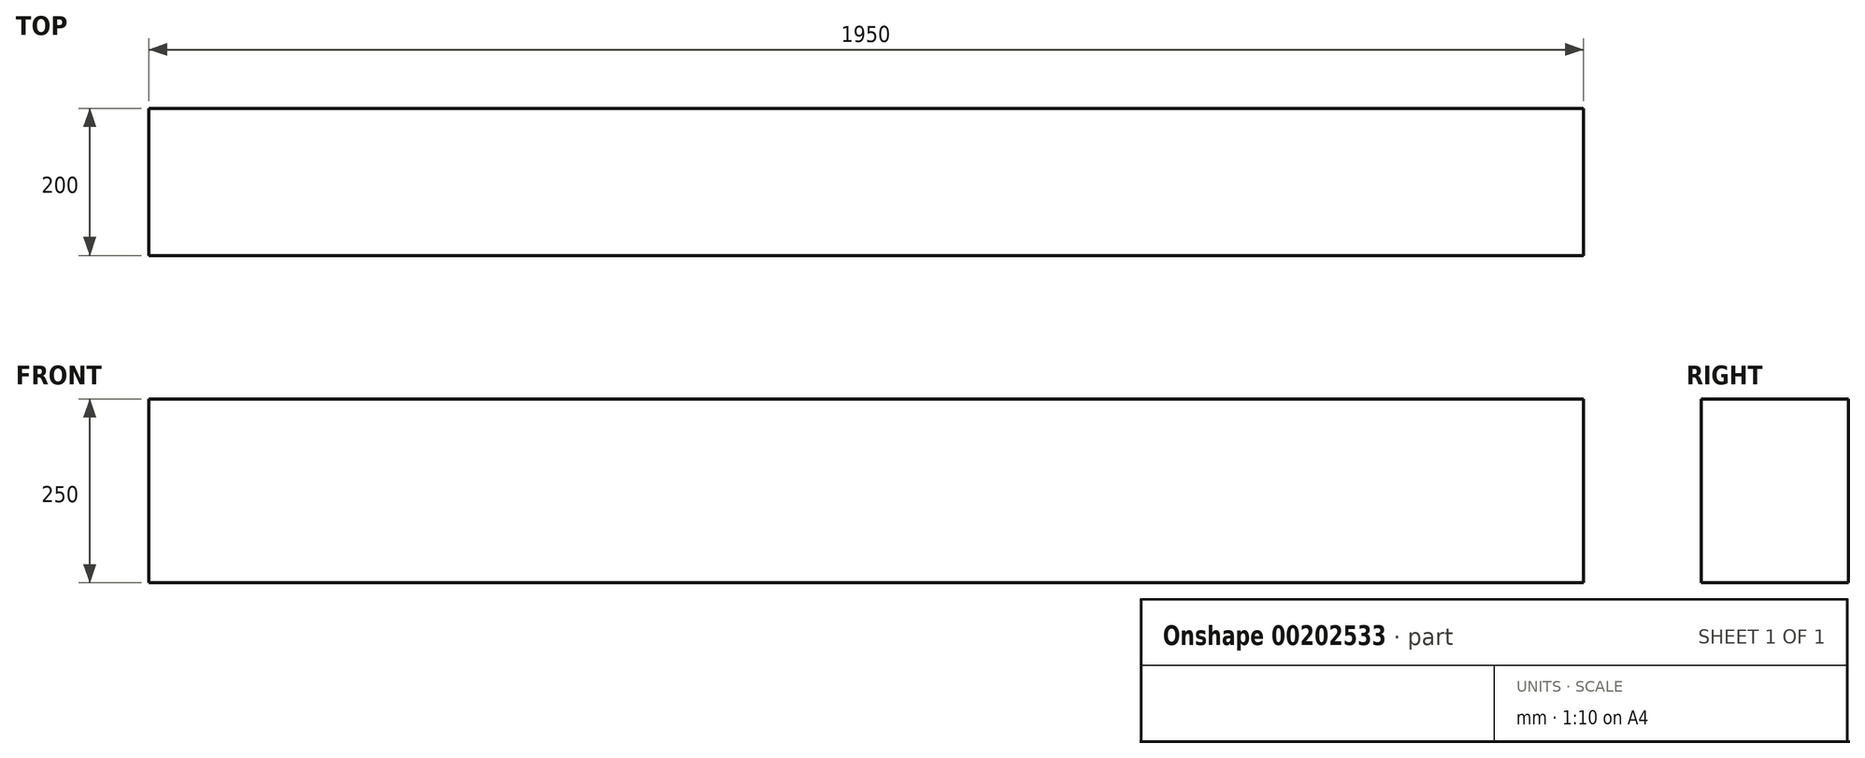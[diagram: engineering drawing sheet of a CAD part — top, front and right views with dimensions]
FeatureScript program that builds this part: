
annotation { "Feature Type Name" : "Feature", "Feature Type Description" : "" }
export const myFeature = defineFeature(function(context is Context, id is Id, definition is map)
    precondition{}
    {
        {
            var Q0;
            Q0=qCreatedBy(makeId("Top.planeOp"),FACE);
            var sketch = newSketch(context, id + "F0", { "sketchPlane" : qUnion([Q0])});
            skLineSegment(sketch, "E0.bottom", {"start": v(-1052.54, -347.66) * mm, "end": v(897.46, -347.66) * mm});
            skLineSegment(sketch, "E0.top", {"start": v(-1052.54, -147.66) * mm, "end": v(897.46, -147.66) * mm});
            skLineSegment(sketch, "E0.left", {"start": v(-1052.54, -347.66) * mm, "end": v(-1052.54, -147.66) * mm});
            skLineSegment(sketch, "E0.right", {"start": v(897.46, -347.66) * mm, "end": v(897.46, -147.66) * mm});
            skSolve(sketch);
        }
        {
            var Q0;
            Q0=makeQuery(id+"F0.imprint","IMPRINT",FACE,{"disambiguationData":[TD([[makeQuery(id+"F0.imprint","IMPRINT",EDGE,{"derivedFrom":sQuery(id+"F0.wireOp",EDGE,"E0.bottom")}),1.0]])]});
            extrude(context, id + "F1", {"entities" : qUnion([Q0]), "depth" : 250 * mm});
        }
    });
